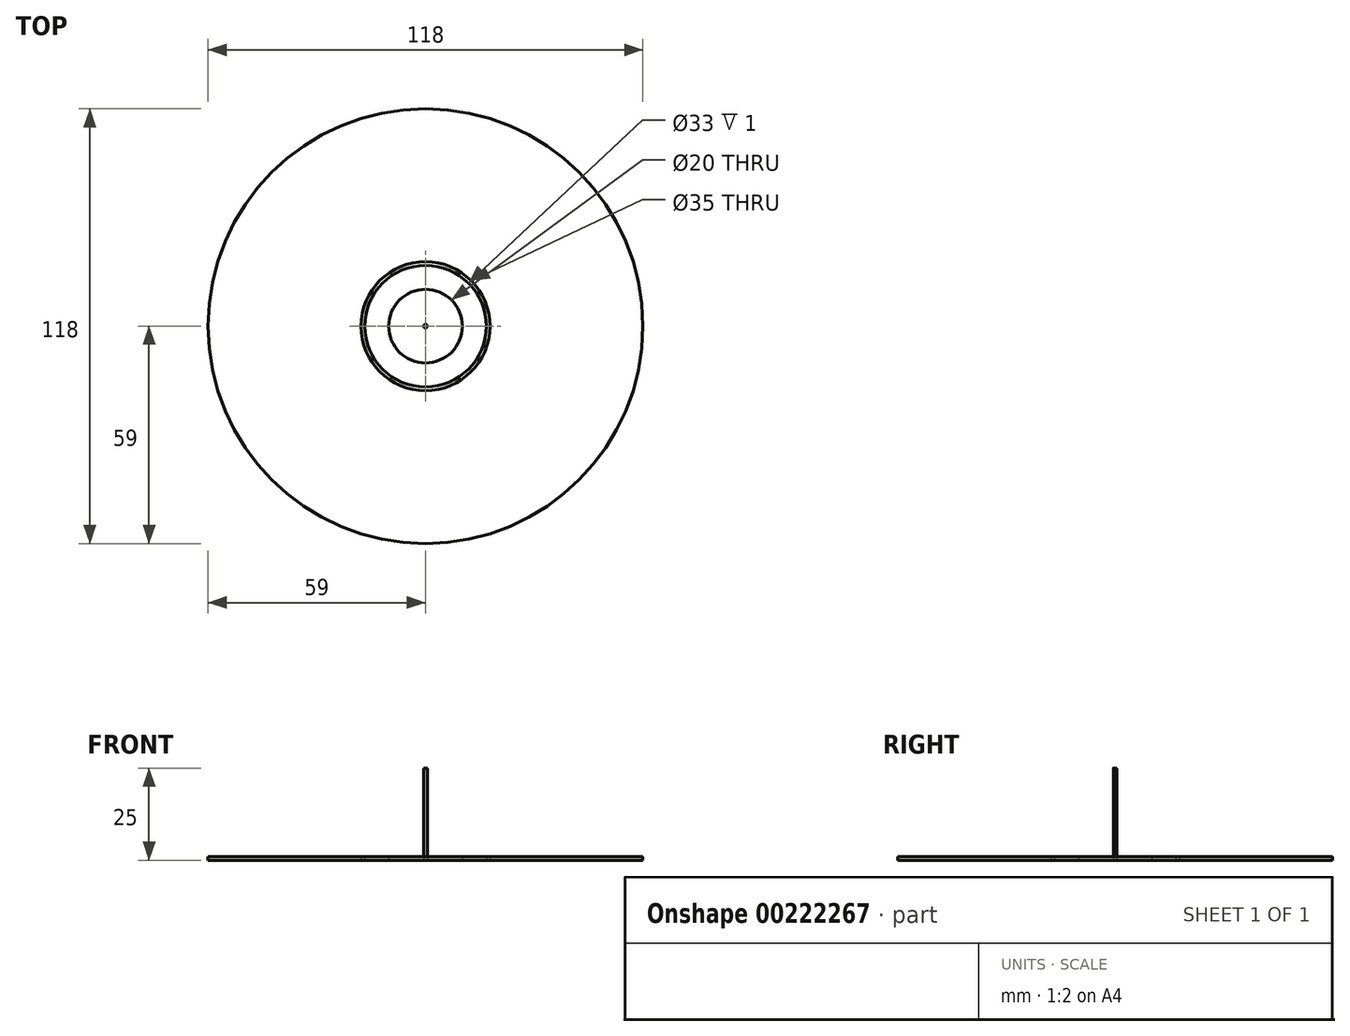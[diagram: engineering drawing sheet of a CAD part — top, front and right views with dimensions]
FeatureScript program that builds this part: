
annotation { "Feature Type Name" : "Feature", "Feature Type Description" : "" }
export const myFeature = defineFeature(function(context is Context, id is Id, definition is map)
    precondition{}
    {
        {
            var Q0;
            Q0=qCreatedBy(makeId("Top.planeOp"),FACE);
            var sketch = newSketch(context, id + "F0", { "sketchPlane" : qUnion([Q0])});
            skCircle(sketch, "E0", {"center": v(0, 0) * mm, "radius": 59 * mm});
            skCircle(sketch, "E1", {"center": v(0, 0) * mm, "radius": 10 * mm});
            skCircle(sketch, "E2", {"center": v(0, 0) * mm, "radius": 16.5 * mm});
            skCircle(sketch, "E3", {"center": v(0, 0) * mm, "radius": 17.5 * mm});
            skSolve(sketch);
        }
        {
            var Q0;
            Q0=makeQuery(id+"F0.imprint","IMPRINT",FACE,{"disambiguationData":[TD([[makeQuery(id+"F0.imprint","IMPRINT",EDGE,{"derivedFrom":sQuery(id+"F0.wireOp",EDGE,"E0")}),1.0]])]});
            extrude(context, id + "F1", {"entities" : qUnion([Q0]), "depth" : 1 * mm});
        }
        {
            var Q0;
            Q0=qCreatedBy(makeId("Top.planeOp"),FACE);
            var sketch = newSketch(context, id + "F2", { "sketchPlane" : qUnion([Q0])});
            skCircle(sketch, "E4", {"center": v(0, 0) * mm, "radius": 0.5 * mm});
            skSolve(sketch);
        }
        {
            var Q0;
            Q0=makeQuery(id+"F2.imprint","IMPRINT",FACE,{"disambiguationData":[TD([[makeQuery(id+"F2.imprint","IMPRINT",EDGE,{"derivedFrom":sQuery(id+"F2.wireOp",EDGE,"E4")}),1.0]])]});
            extrude(context, id + "F3", {"entities" : qUnion([Q0]), "depth" : 25 * mm});
        }
        {
            var Q0;
            Q0=makeQuery(id+"F0.imprint","IMPRINT",FACE,{"disambiguationData":[TD([[makeQuery(id+"F0.imprint","IMPRINT",EDGE,{"derivedFrom":sQuery(id+"F0.wireOp",EDGE,"E1")}),-1.0]])]});
            extrude(context, id + "F4", {"entities" : qUnion([Q0]), "depth" : 1 * mm});
        }
        {
            var Q0;
            Q0=makeQuery(id+"F0.imprint","IMPRINT",FACE,{"disambiguationData":[TD([[makeQuery(id+"F0.imprint","IMPRINT",EDGE,{"derivedFrom":sQuery(id+"F0.wireOp",EDGE,"E2")}),-1.0]])]});
            extrude(context, id + "F5", {"entities" : qUnion([Q0]), "depth" : 1 * mm});
        }
    });
